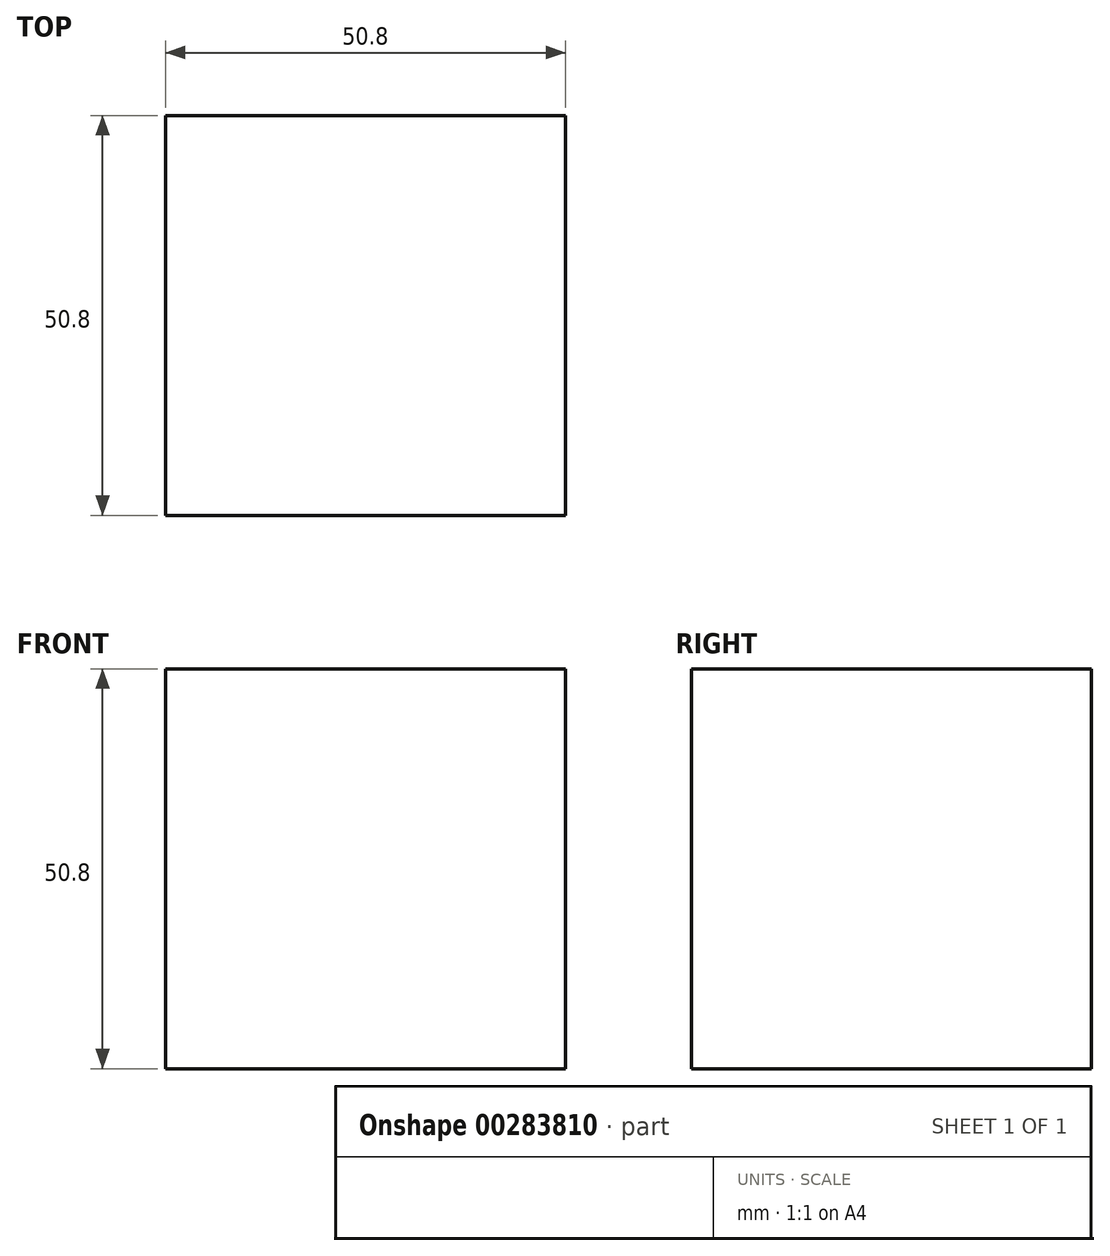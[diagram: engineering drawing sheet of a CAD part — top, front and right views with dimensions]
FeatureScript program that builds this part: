
annotation { "Feature Type Name" : "Feature", "Feature Type Description" : "" }
export const myFeature = defineFeature(function(context is Context, id is Id, definition is map)
    precondition{}
    {
        {
            var Q0;
            Q0=qCreatedBy(makeId("Front.planeOp"),FACE);
            var sketch = newSketch(context, id + "F0", { "sketchPlane" : qUnion([Q0])});
            skLineSegment(sketch, "E0.bottom", {"start": v(0, 0) * mm, "end": v(50.8, 0) * mm});
            skLineSegment(sketch, "E0.top", {"start": v(0, 50.8) * mm, "end": v(50.8, 50.8) * mm});
            skLineSegment(sketch, "E0.left", {"start": v(0, 0) * mm, "end": v(0, 50.8) * mm});
            skLineSegment(sketch, "E0.right", {"start": v(50.8, 0) * mm, "end": v(50.8, 50.8) * mm});
            skSolve(sketch);
        }
        {
            var Q0;
            Q0 = qSketchRegion(id + "F0", true);
            var Q1;
            Q1=makeQuery(id+"F0.imprint","IMPRINT",FACE,{"disambiguationData":[TD([[makeQuery(id+"F0.imprint","IMPRINT",EDGE,{"derivedFrom":sQuery(id+"F0.wireOp",EDGE,"E0.bottom")}),1.0]])]});
            extrude(context, id + "F1", {"entities" : qUnion([Q0, Q1]), "depth" : 50.8 * mm});
        }
    });
